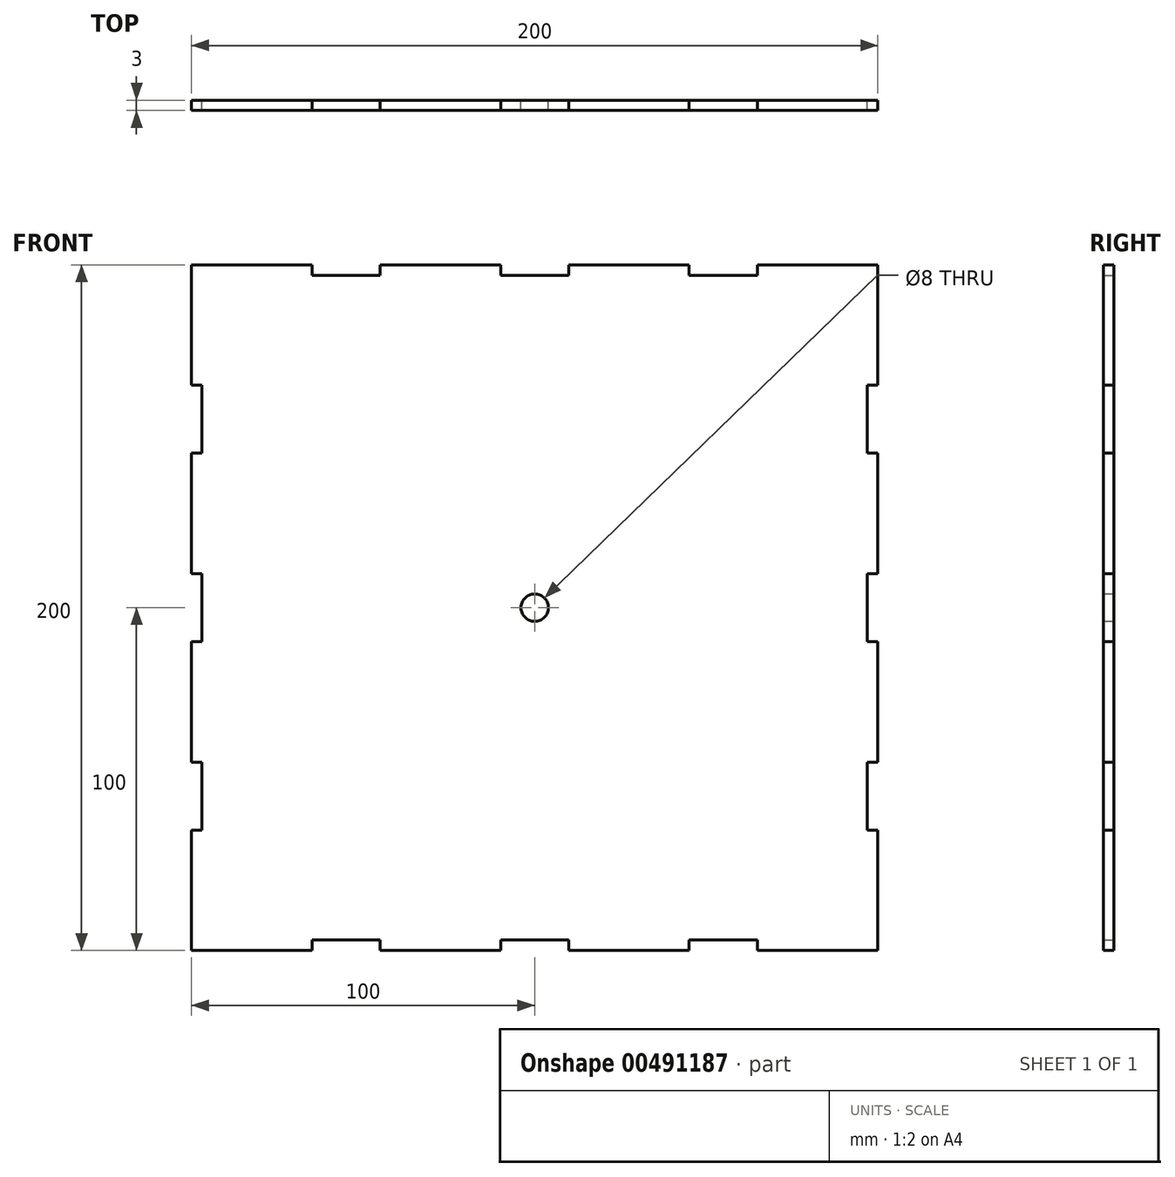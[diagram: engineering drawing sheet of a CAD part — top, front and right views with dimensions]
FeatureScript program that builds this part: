
annotation { "Feature Type Name" : "Feature", "Feature Type Description" : "" }
export const myFeature = defineFeature(function(context is Context, id is Id, definition is map)
    precondition{}
    {
        {
            var Q0;
            Q0=qCreatedBy(makeId("Front.planeOp"),FACE);
            var sketch = newSketch(context, id + "F0", { "sketchPlane" : qUnion([Q0])});
            skLineSegment(sketch, "E0.bottom", {"start": v(100, -100) * mm, "end": v(-100, -100) * mm});
            skLineSegment(sketch, "E0.top", {"start": v(100, 100) * mm, "end": v(-100, 100) * mm});
            skLineSegment(sketch, "E0.left", {"start": v(100, -100) * mm, "end": v(100, 100) * mm});
            skLineSegment(sketch, "E0.right", {"start": v(-100, -100) * mm, "end": v(-100, 100) * mm});
            skPoint(sketch, "E0.middle", {"position": v(0, 0) * mm});
            skCircle(sketch, "E1", {"center": v(0, 0) * mm, "radius": 4 * mm});
            skLineSegment(sketch, "E2.bottom", {"start": v(-45.03, -100) * mm, "end": v(-64.93, -100) * mm});
            skLineSegment(sketch, "E2.top", {"start": v(-45.03, -96.95) * mm, "end": v(-64.93, -96.95) * mm});
            skLineSegment(sketch, "E2.left", {"start": v(-45.03, -100) * mm, "end": v(-45.03, -96.95) * mm});
            skLineSegment(sketch, "E2.right", {"start": v(-64.93, -100) * mm, "end": v(-64.93, -96.95) * mm});
            skPoint(sketch, "E2.middle", {"position": v(-54.98, -98.47) * mm});
            skLineSegment(sketch, "E3.bottom", {"start": v(45.02, -100) * mm, "end": v(64.92, -100) * mm});
            skLineSegment(sketch, "E3.top", {"start": v(45.02, -96.95) * mm, "end": v(64.92, -96.95) * mm});
            skLineSegment(sketch, "E3.left", {"start": v(45.02, -100) * mm, "end": v(45.02, -96.95) * mm});
            skLineSegment(sketch, "E3.right", {"start": v(64.92, -100) * mm, "end": v(64.92, -96.95) * mm});
            skPoint(sketch, "E3.middle", {"position": v(54.97, -98.48) * mm});
            skLineSegment(sketch, "E4.bottom", {"start": v(9.95, -100) * mm, "end": v(-9.95, -100) * mm});
            skLineSegment(sketch, "E4.top", {"start": v(9.95, -96.95) * mm, "end": v(-9.95, -96.95) * mm});
            skLineSegment(sketch, "E4.left", {"start": v(9.95, -100) * mm, "end": v(9.95, -96.95) * mm});
            skLineSegment(sketch, "E4.right", {"start": v(-9.95, -100) * mm, "end": v(-9.95, -96.95) * mm});
            skPoint(sketch, "E4.middle", {"position": v(0, -98.47) * mm});
            skLineSegment(sketch, "E5.bottom", {"start": v(-100, -45.03) * mm, "end": v(-96.95, -45.03) * mm});
            skLineSegment(sketch, "E5.top", {"start": v(-100, -64.93) * mm, "end": v(-96.95, -64.93) * mm});
            skLineSegment(sketch, "E5.left", {"start": v(-100, -45.03) * mm, "end": v(-100, -64.93) * mm});
            skLineSegment(sketch, "E5.right", {"start": v(-96.95, -45.03) * mm, "end": v(-96.95, -64.93) * mm});
            skPoint(sketch, "E5.middle", {"position": v(-98.48, -54.98) * mm});
            skLineSegment(sketch, "E6.bottom", {"start": v(-96.95, -9.95) * mm, "end": v(-100, -9.95) * mm});
            skLineSegment(sketch, "E6.top", {"start": v(-96.95, 9.95) * mm, "end": v(-100, 9.95) * mm});
            skLineSegment(sketch, "E6.left", {"start": v(-96.95, -9.95) * mm, "end": v(-96.95, 9.95) * mm});
            skLineSegment(sketch, "E6.right", {"start": v(-100, -9.95) * mm, "end": v(-100, 9.95) * mm});
            skPoint(sketch, "E6.middle", {"position": v(-98.48, 0) * mm});
            skLineSegment(sketch, "E7.bottom", {"start": v(-96.95, 45.02) * mm, "end": v(-100, 45.02) * mm});
            skLineSegment(sketch, "E7.top", {"start": v(-96.95, 64.92) * mm, "end": v(-100, 64.92) * mm});
            skLineSegment(sketch, "E7.left", {"start": v(-96.95, 45.02) * mm, "end": v(-96.95, 64.92) * mm});
            skLineSegment(sketch, "E7.right", {"start": v(-100, 45.02) * mm, "end": v(-100, 64.92) * mm});
            skPoint(sketch, "E7.middle", {"position": v(-98.48, 54.97) * mm});
            skLineSegment(sketch, "E8.bottom", {"start": v(100, 45.03) * mm, "end": v(96.95, 45.03) * mm});
            skLineSegment(sketch, "E8.top", {"start": v(100, 64.93) * mm, "end": v(96.95, 64.93) * mm});
            skLineSegment(sketch, "E8.left", {"start": v(100, 45.03) * mm, "end": v(100, 64.93) * mm});
            skLineSegment(sketch, "E8.right", {"start": v(96.95, 45.03) * mm, "end": v(96.95, 64.93) * mm});
            skPoint(sketch, "E8.middle", {"position": v(98.48, 54.98) * mm});
            skLineSegment(sketch, "E9.bottom", {"start": v(100, -9.95) * mm, "end": v(96.95, -9.95) * mm});
            skLineSegment(sketch, "E9.top", {"start": v(100, 9.95) * mm, "end": v(96.95, 9.95) * mm});
            skLineSegment(sketch, "E9.left", {"start": v(100, -9.95) * mm, "end": v(100, 9.95) * mm});
            skLineSegment(sketch, "E9.right", {"start": v(96.95, -9.95) * mm, "end": v(96.95, 9.95) * mm});
            skPoint(sketch, "E9.middle", {"position": v(98.47, 0) * mm});
            skLineSegment(sketch, "E10.bottom", {"start": v(100, -64.92) * mm, "end": v(96.95, -64.92) * mm});
            skLineSegment(sketch, "E10.top", {"start": v(100, -45.02) * mm, "end": v(96.95, -45.02) * mm});
            skLineSegment(sketch, "E10.left", {"start": v(100, -64.92) * mm, "end": v(100, -45.02) * mm});
            skLineSegment(sketch, "E10.right", {"start": v(96.95, -64.92) * mm, "end": v(96.95, -45.02) * mm});
            skPoint(sketch, "E10.middle", {"position": v(98.47, -54.97) * mm});
            skLineSegment(sketch, "E11.bottom", {"start": v(-45.03, 100) * mm, "end": v(-64.93, 100) * mm});
            skLineSegment(sketch, "E11.top", {"start": v(-45.03, 96.95) * mm, "end": v(-64.93, 96.95) * mm});
            skLineSegment(sketch, "E11.left", {"start": v(-45.03, 100) * mm, "end": v(-45.03, 96.95) * mm});
            skLineSegment(sketch, "E11.right", {"start": v(-64.93, 100) * mm, "end": v(-64.93, 96.95) * mm});
            skPoint(sketch, "E11.middle", {"position": v(-54.98, 98.47) * mm});
            skLineSegment(sketch, "E12.bottom", {"start": v(9.95, 96.95) * mm, "end": v(-9.95, 96.95) * mm});
            skLineSegment(sketch, "E12.top", {"start": v(9.95, 100) * mm, "end": v(-9.95, 100) * mm});
            skLineSegment(sketch, "E12.left", {"start": v(9.95, 96.95) * mm, "end": v(9.95, 100) * mm});
            skLineSegment(sketch, "E12.right", {"start": v(-9.95, 96.95) * mm, "end": v(-9.95, 100) * mm});
            skPoint(sketch, "E12.middle", {"position": v(0, 98.48) * mm});
            skLineSegment(sketch, "E13.bottom", {"start": v(64.93, 96.95) * mm, "end": v(45.03, 96.95) * mm});
            skLineSegment(sketch, "E13.top", {"start": v(64.93, 100) * mm, "end": v(45.03, 100) * mm});
            skLineSegment(sketch, "E13.left", {"start": v(64.93, 96.95) * mm, "end": v(64.93, 100) * mm});
            skLineSegment(sketch, "E13.right", {"start": v(45.03, 96.95) * mm, "end": v(45.03, 100) * mm});
            skPoint(sketch, "E13.middle", {"position": v(54.98, 98.48) * mm});
            skSolve(sketch);
        }
        {
            var Q0;
            Q0=makeQuery(id+"F0.imprint","IMPRINT",FACE,{"disambiguationData":[TD([[makeQuery(id+"F0.imprint","IMPRINT",EDGE,{"derivedFrom":sQuery(id+"F0.wireOp",EDGE,"E0.top")}),1.0]])]});
            extrude(context, id + "F1", {"entities" : qUnion([Q0]), "depth" : 3 * mm});
        }
    });
